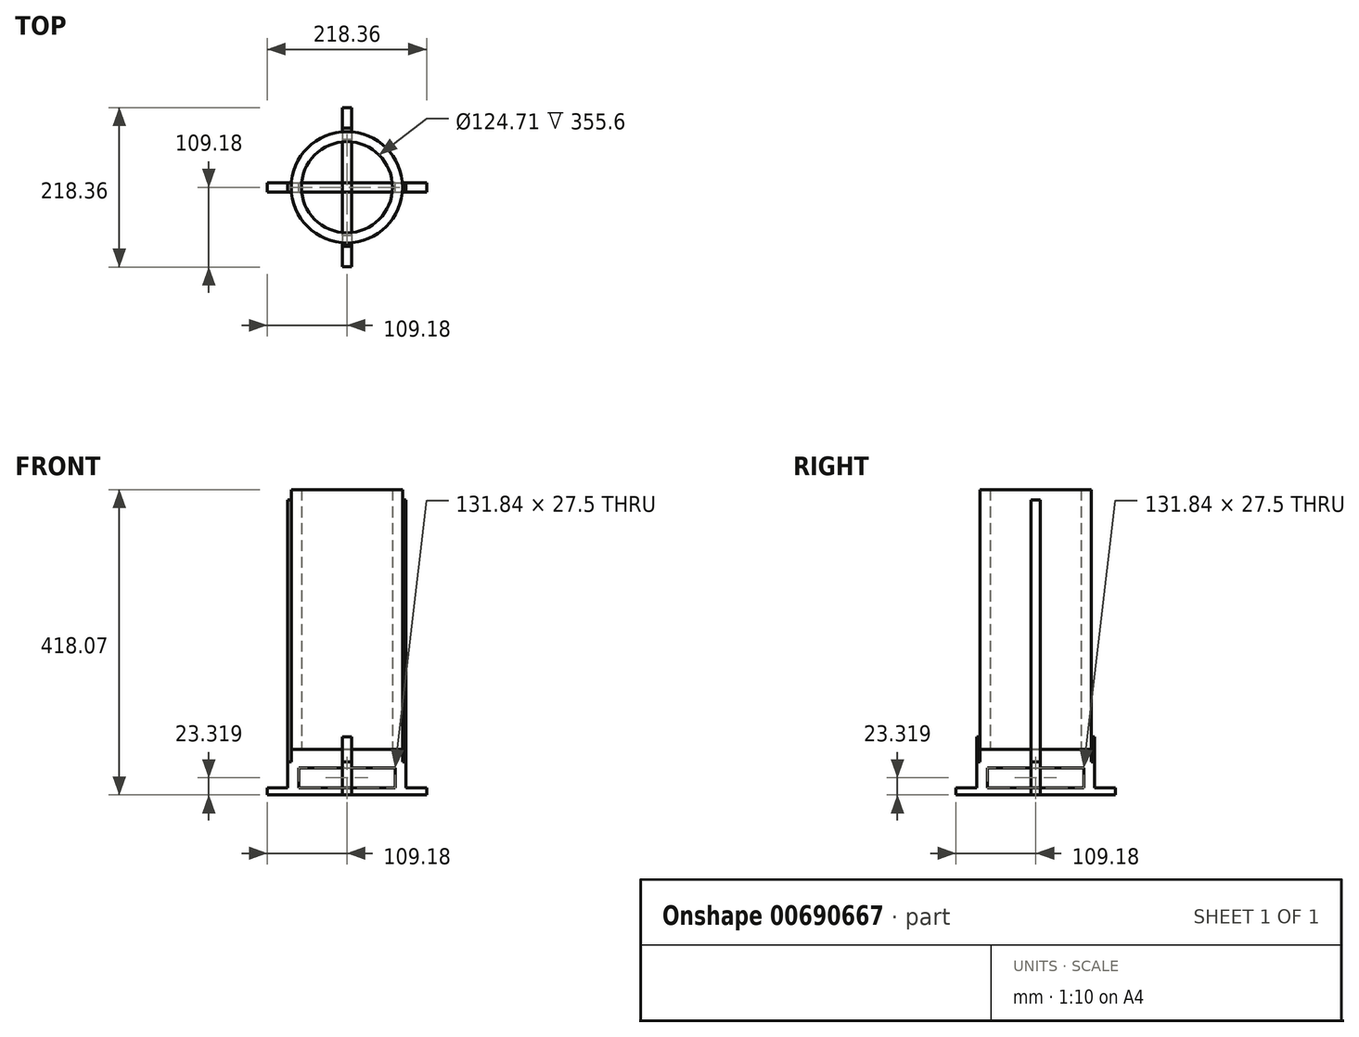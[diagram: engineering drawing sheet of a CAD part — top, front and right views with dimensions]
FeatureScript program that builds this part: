
annotation { "Feature Type Name" : "Feature", "Feature Type Description" : "" }
export const myFeature = defineFeature(function(context is Context, id is Id, definition is map)
    precondition{}
    {
        {
            var Q0;
            Q0=qCreatedBy(makeId("Top.planeOp"),FACE);
            var sketch = newSketch(context, id + "F0", { "sketchPlane" : qUnion([Q0])});
            skCircle(sketch, "E0", {"center": v(0, 0) * mm, "radius": 76.2 * mm});
            skCircle(sketch, "E1.0", {"center": v(0, 0) * mm, "radius": 62.36 * mm});
            skSolve(sketch);
        }
        {
            var Q0;
            Q0=qSketchRegion(id+"F0",true);
            extrude(context, id + "F1", {"entities" : qUnion([Q0]), "depth" : 355.6 * mm, "offsetDistance" : 25.4 * mm});
        }
        {
            var Q0;
            Q0=qCreatedBy(makeId("Front.planeOp"),FACE);
            var sketch = newSketch(context, id + "F2", { "sketchPlane" : qUnion([Q0])});
            skLineSegment(sketch, "E2", {"start": v(0, 0) * mm, "end": v(76.2, 0) * mm});
            skLineSegment(sketch, "E3", {"start": v(65.92, -52.9) * mm, "end": v(65.92, -25.4) * mm});
            skLineSegment(sketch, "E4", {"start": v(65.92, -25.4) * mm, "end": v(0, -25.4) * mm});
            skLineSegment(sketch, "E5", {"start": v(76.2, 0) * mm, "end": v(76.2, -16.95) * mm});
            skLineSegment(sketch, "E6", {"start": v(76.2, -16.95) * mm, "end": v(80.84, -16.95) * mm});
            skLineSegment(sketch, "E7", {"start": v(80.84, -16.95) * mm, "end": v(80.84, -52.9) * mm});
            skLineSegment(sketch, "E8", {"start": v(0, 0) * mm, "end": v(0, -25.4) * mm});
            skLineSegment(sketch, "E9", {"start": v(80.84, -52.9) * mm, "end": v(65.92, -52.9) * mm});
            skLineSegment(sketch, "E10.bottom", {"start": v(0, -52.9) * mm, "end": v(0, -52.9) * mm});
            skLineSegment(sketch, "E10.left", {"start": v(0, -52.9) * mm, "end": v(0, -62.47) * mm});
            skLineSegment(sketch, "E10.right", {"start": v(0, -52.9) * mm, "end": v(0, -62.47) * mm});
            skLineSegment(sketch, "E11.bottom", {"start": v(0, -52.9) * mm, "end": v(109.18, -52.9) * mm});
            skLineSegment(sketch, "E11.top", {"start": v(0, -62.47) * mm, "end": v(109.18, -62.47) * mm});
            skLineSegment(sketch, "E11.right", {"start": v(109.18, -52.9) * mm, "end": v(109.18, -62.47) * mm});
            skLineSegment(sketch, "E12.MirrorCS", {"start": v(-76.2, -16.95) * mm, "end": v(-80.84, -16.95) * mm});
            skLineSegment(sketch, "E13.MirrorCS", {"start": v(-76.2, 0) * mm, "end": v(-76.2, -16.95) * mm});
            skLineSegment(sketch, "E14.MirrorCS", {"start": v(-80.84, -52.9) * mm, "end": v(-65.92, -52.9) * mm});
            skLineSegment(sketch, "E15.MirrorCS", {"start": v(-109.18, -52.9) * mm, "end": v(-109.18, -62.47) * mm});
            skLineSegment(sketch, "E16.MirrorCS", {"start": v(-65.92, -25.4) * mm, "end": v(0, -25.4) * mm});
            skLineSegment(sketch, "E17.MirrorCS", {"start": v(0, -52.9) * mm, "end": v(-109.18, -52.9) * mm});
            skLineSegment(sketch, "E18.MirrorCS", {"start": v(0, -62.47) * mm, "end": v(-109.18, -62.47) * mm});
            skLineSegment(sketch, "E19.MirrorCS", {"start": v(-65.92, -52.9) * mm, "end": v(-65.92, -25.4) * mm});
            skLineSegment(sketch, "E20.MirrorCS", {"start": v(0, 0) * mm, "end": v(-76.2, 0) * mm});
            skLineSegment(sketch, "E21.MirrorCS", {"start": v(-80.84, -16.95) * mm, "end": v(-80.84, -52.9) * mm});
            skSolve(sketch);
        }
        {
            var Q0;
            Q0=qSketchRegion(id+"F2",true);
            extrude(context, id + "F3", {"entities" : qUnion([Q0]), "endBound" : BoundingType.SYMMETRIC, "depth" : 12.7 * mm, "offsetDistance" : 25.4 * mm});
        }
        {
            var Q0;
            Q0=makeQuery(id+"F3.opExtrude","SWEPT_BODY",BODY,{"disambiguationData":[OSD([sQuery(id+"F2.wireOp",EDGE,"E2"),sQuery(id+"F2.wireOp",EDGE,"E3"),sQuery(id+"F2.wireOp",EDGE,"E4"),sQuery(id+"F2.wireOp",EDGE,"E5"),sQuery(id+"F2.wireOp",EDGE,"E6"),sQuery(id+"F2.wireOp",EDGE,"E7"),sQuery(id+"F2.wireOp",EDGE,"yYa1QQtk-rfeQ-uA0k-yN95-LENgFDuBBmhA"),sQuery(id+"F2.wireOp",EDGE,"RaL1Y38n-DL0R-HpUy-0Yu0-hKOuieMtGCDP"),sQuery(id+"F2.wireOp",EDGE,"KzeCX9vK-PA9l-fBDc-L8z4-hnWVkcK37siH"),sQuery(id+"F2.wireOp",EDGE,"7a3115bd-42c9-43fa-886f-b7d7f014f3800.MirrorCS"),sQuery(id+"F2.wireOp",EDGE,"93714e8b-1b55-43fa-9f0a-1818bfe9d4330.MirrorCS"),sQuery(id+"F2.wireOp",EDGE,"f685ec73-5cd7-40c9-a0cc-09a82770efb00.MirrorCS"),sQuery(id+"F2.wireOp",EDGE,"605de593-ab4b-4a38-8b95-8d2e6ad95e7e0.MirrorCS"),sQuery(id+"F2.wireOp",EDGE,"bd68596d-ea5b-43b6-8ec0-eaa4091035650.MirrorCS"),sQuery(id+"F2.wireOp",EDGE,"6dadb6d6-938b-41b2-89eb-21b29489f2620.MirrorCS"),sQuery(id+"F2.wireOp",EDGE,"35a6b2d6-89f1-42be-bee9-e52b24f0a85c0.MirrorCS"),sQuery(id+"F2.wireOp",EDGE,"99d46e2b-beb4-45a8-a67b-b38dd53197940.MirrorCS"),sQuery(id+"F2.wireOp",EDGE,"687b68df-4fec-4741-9a90-ace4315f9af80.MirrorCS")])]});
            transform(context, id + "F4", {"entities" : qUnion([Q0]), "transformType" : TransformType.COPY});
        }
        {
            var Q0;
            Q0=makeQuery(id+"F3.opExtrude","SWEPT_BODY",BODY,{"disambiguationData":[OSD([sQuery(id+"F2.wireOp",EDGE,"E2"),sQuery(id+"F2.wireOp",EDGE,"E3"),sQuery(id+"F2.wireOp",EDGE,"E4"),sQuery(id+"F2.wireOp",EDGE,"E5"),sQuery(id+"F2.wireOp",EDGE,"E6"),sQuery(id+"F2.wireOp",EDGE,"E7"),sQuery(id+"F2.wireOp",EDGE,"yYa1QQtk-rfeQ-uA0k-yN95-LENgFDuBBmhA"),sQuery(id+"F2.wireOp",EDGE,"RaL1Y38n-DL0R-HpUy-0Yu0-hKOuieMtGCDP"),sQuery(id+"F2.wireOp",EDGE,"KzeCX9vK-PA9l-fBDc-L8z4-hnWVkcK37siH"),sQuery(id+"F2.wireOp",EDGE,"7a3115bd-42c9-43fa-886f-b7d7f014f3800.MirrorCS"),sQuery(id+"F2.wireOp",EDGE,"93714e8b-1b55-43fa-9f0a-1818bfe9d4330.MirrorCS"),sQuery(id+"F2.wireOp",EDGE,"f685ec73-5cd7-40c9-a0cc-09a82770efb00.MirrorCS"),sQuery(id+"F2.wireOp",EDGE,"605de593-ab4b-4a38-8b95-8d2e6ad95e7e0.MirrorCS"),sQuery(id+"F2.wireOp",EDGE,"bd68596d-ea5b-43b6-8ec0-eaa4091035650.MirrorCS"),sQuery(id+"F2.wireOp",EDGE,"6dadb6d6-938b-41b2-89eb-21b29489f2620.MirrorCS"),sQuery(id+"F2.wireOp",EDGE,"35a6b2d6-89f1-42be-bee9-e52b24f0a85c0.MirrorCS"),sQuery(id+"F2.wireOp",EDGE,"99d46e2b-beb4-45a8-a67b-b38dd53197940.MirrorCS"),sQuery(id+"F2.wireOp",EDGE,"687b68df-4fec-4741-9a90-ace4315f9af80.MirrorCS")])]});
            var Q1;
            Q1=sQuery(id+"F2.wireOp",EDGE,"E8");
            transform(context, id + "F5", {"entities" : qUnion([Q0]), "transformType" : TransformType.ROTATION, "transformAxis" : qUnion([Q1]), "angle" : 90 * degree, "makeCopy" : false});
        }
        {
            var Q0;
            Q0=makeQuery(id+"F4.opPattern","COPY",FACE,{"derivedFrom":makeQuery(id+"F3.opExtrude","CAP_FACE",FACE,{"disambiguationData":[OSD([sQuery(id+"F2.wireOp",EDGE,"E2"),sQuery(id+"F2.wireOp",EDGE,"E3"),sQuery(id+"F2.wireOp",EDGE,"E4"),sQuery(id+"F2.wireOp",EDGE,"E5"),sQuery(id+"F2.wireOp",EDGE,"E6"),sQuery(id+"F2.wireOp",EDGE,"E7"),sQuery(id+"F2.wireOp",EDGE,"E11.bottom"),sQuery(id+"F2.wireOp",EDGE,"E11.top"),sQuery(id+"F2.wireOp",EDGE,"E11.right"),sQuery(id+"F2.wireOp",EDGE,"6d3937cc-c99b-4de3-b3db-85ad403e89ce3.MirrorCS"),sQuery(id+"F2.wireOp",EDGE,"E15.MirrorCS"),sQuery(id+"F2.wireOp",EDGE,"6d3937cc-c99b-4de3-b3db-85ad403e89ce8.MirrorCS"),sQuery(id+"F2.wireOp",EDGE,"E16.MirrorCS"),sQuery(id+"F2.wireOp",EDGE,"E17.MirrorCS"),sQuery(id+"F2.wireOp",EDGE,"E18.MirrorCS"),sQuery(id+"F2.wireOp",EDGE,"E19.MirrorCS"),sQuery(id+"F2.wireOp",EDGE,"E20.MirrorCS"),sQuery(id+"F2.wireOp",EDGE,"6d3937cc-c99b-4de3-b3db-85ad403e89ce15.MirrorCS"),sQuery(id+"F2.wireOp",EDGE,"E21.MirrorCS")])],"isStart":false}),"instanceName":"1"});
            var sketch = newSketch(context, id + "F6", { "sketchPlane" : qUnion([Q0])});
            skLineSegment(sketch, "E22.bottom", {"start": v(76.2, -16.95) * mm, "end": v(80.84, -16.95) * mm});
            skLineSegment(sketch, "E22.top", {"start": v(76.2, 341.82) * mm, "end": v(80.84, 341.82) * mm});
            skLineSegment(sketch, "E22.left", {"start": v(76.2, -16.95) * mm, "end": v(76.2, 341.82) * mm});
            skLineSegment(sketch, "E22.right", {"start": v(80.84, -16.95) * mm, "end": v(80.84, 341.82) * mm});
            skSolve(sketch);
        }
        {
            var Q0;
            {var subQ3=sQuery(id+"F6.wireOp",EDGE,"E22.bottom");Q0=makeQuery(id+"F6.imprint","IMPRINT",FACE,{"disambiguationData":[TD([[makeQuery(id+"F6.imprint","IMPRINT",EDGE,{"derivedFrom":subQ3}),1.0]])]});}
            extrude(context, id + "F7", {"entities" : qUnion([Q0]), "oppositeDirection" : true, "depth" : 12.7 * mm, "offsetDistance" : 25.4 * mm});
        }
        {
            var Q0;
            Q0=makeQuery(id+"F7.opExtrude","SWEPT_BODY",BODY,{"disambiguationData":[OSD([sQuery(id+"F6.wireOp",EDGE,"E22.bottom"),sQuery(id+"F6.wireOp",EDGE,"E22.top"),sQuery(id+"F6.wireOp",EDGE,"E22.left"),sQuery(id+"F6.wireOp",EDGE,"E22.right")])]});
            var Q1;
            Q1=sQuery(id+"F2.wireOp",EDGE,"E8");
            circularPattern(context, id + "F8", {"entities" : qUnion([Q0]), "axis" : qUnion([Q1]), "angle" : 360 * degree, "instanceCount" : 2, "equalSpace" : true});
        }
        {
            var Q0;
            Q0=makeQuery(id+"F3.opExtrude","CAP_FACE",FACE,{"disambiguationData":[OSD([sQuery(id+"F2.wireOp",EDGE,"E2"),sQuery(id+"F2.wireOp",EDGE,"E3"),sQuery(id+"F2.wireOp",EDGE,"E4"),sQuery(id+"F2.wireOp",EDGE,"E5"),sQuery(id+"F2.wireOp",EDGE,"E6"),sQuery(id+"F2.wireOp",EDGE,"E7"),sQuery(id+"F2.wireOp",EDGE,"E11.bottom"),sQuery(id+"F2.wireOp",EDGE,"E11.top"),sQuery(id+"F2.wireOp",EDGE,"E11.right"),sQuery(id+"F2.wireOp",EDGE,"E12.MirrorCS"),sQuery(id+"F2.wireOp",EDGE,"E13.MirrorCS"),sQuery(id+"F2.wireOp",EDGE,"E15.MirrorCS"),sQuery(id+"F2.wireOp",EDGE,"E16.MirrorCS"),sQuery(id+"F2.wireOp",EDGE,"E17.MirrorCS"),sQuery(id+"F2.wireOp",EDGE,"E18.MirrorCS"),sQuery(id+"F2.wireOp",EDGE,"E19.MirrorCS"),sQuery(id+"F2.wireOp",EDGE,"E20.MirrorCS"),sQuery(id+"F2.wireOp",EDGE,"E21.MirrorCS")])],"isStart":false});
            var sketch = newSketch(context, id + "F9", { "sketchPlane" : qUnion([Q0])});
            skLineSegment(sketch, "E23.bottom", {"start": v(76.2, -16.95) * mm, "end": v(80.84, -16.95) * mm});
            skLineSegment(sketch, "E23.top", {"start": v(76.2, 17.25) * mm, "end": v(80.84, 17.25) * mm});
            skLineSegment(sketch, "E23.left", {"start": v(76.2, -16.95) * mm, "end": v(76.2, 17.25) * mm});
            skLineSegment(sketch, "E23.right", {"start": v(80.84, -16.95) * mm, "end": v(80.84, 17.25) * mm});
            skSolve(sketch);
        }
        {
            var Q0;
            Q0=qSketchRegion(id+"F9",true);
            extrude(context, id + "F10", {"entities" : qUnion([Q0]), "oppositeDirection" : true, "depth" : 12.7 * mm, "offsetDistance" : 25.4 * mm});
        }
        {
            var Q0;
            Q0=makeQuery(id+"F10.opExtrude","SWEPT_BODY",BODY,{"disambiguationData":[OSD([sQuery(id+"F9.wireOp",EDGE,"E23.bottom"),sQuery(id+"F9.wireOp",EDGE,"E23.top"),sQuery(id+"F9.wireOp",EDGE,"E23.left"),sQuery(id+"F9.wireOp",EDGE,"E23.right")])]});
            var Q1;
            Q1=sQuery(id+"F2.wireOp",EDGE,"E8");
            circularPattern(context, id + "F11", {"entities" : qUnion([Q0]), "axis" : qUnion([Q1]), "angle" : 360 * degree, "instanceCount" : 2, "equalSpace" : true});
        }
    });
